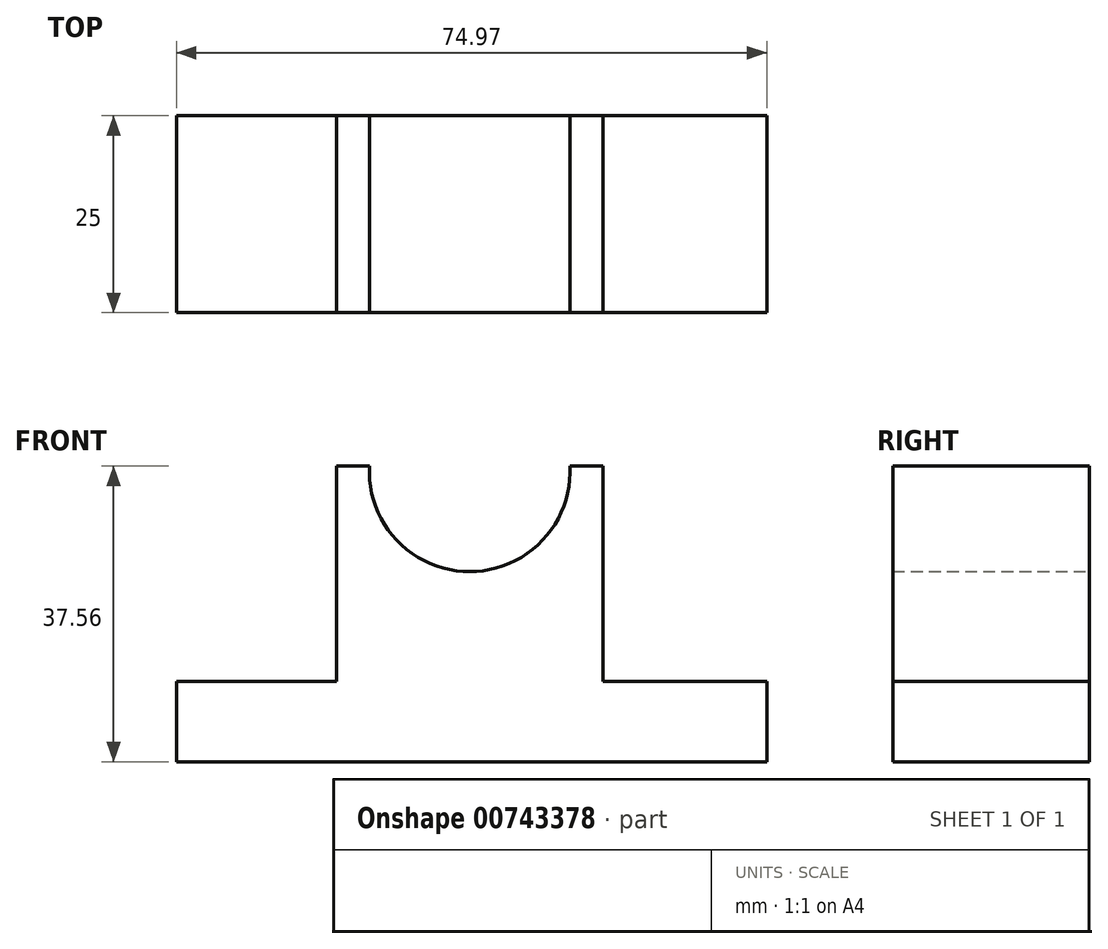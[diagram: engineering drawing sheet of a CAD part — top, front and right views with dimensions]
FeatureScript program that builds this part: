
annotation { "Feature Type Name" : "Feature", "Feature Type Description" : "" }
export const myFeature = defineFeature(function(context is Context, id is Id, definition is map)
    precondition{}
    {
        {
            var Q0;
            Q0=qCreatedBy(makeId("Front.planeOp"),FACE);
            var sketch = newSketch(context, id + "F0", { "sketchPlane" : qUnion([Q0])});
            skLineSegment(sketch, "E0", {"start": v(0, 0) * mm, "end": v(0, 10.22) * mm});
            skLineSegment(sketch, "E1", {"start": v(0, 0) * mm, "end": v(74.97, 0) * mm});
            skLineSegment(sketch, "E2", {"start": v(74.97, 0) * mm, "end": v(74.97, 10.22) * mm});
            skLineSegment(sketch, "E3", {"start": v(0, 10.22) * mm, "end": v(20.3, 10.22) * mm});
            skLineSegment(sketch, "E4", {"start": v(74.97, 10.22) * mm, "end": v(54.13, 10.22) * mm});
            skLineSegment(sketch, "E5", {"start": v(54.13, 10.22) * mm, "end": v(54.13, 37.56) * mm});
            skLineSegment(sketch, "E6", {"start": v(20.3, 10.22) * mm, "end": v(20.3, 37.56) * mm});
            skLineSegment(sketch, "E7", {"start": v(20.3, 37.56) * mm, "end": v(24.5, 37.56) * mm});
            skLineSegment(sketch, "E8", {"start": v(54.13, 37.56) * mm, "end": v(49.96, 37.56) * mm});
            skArc(sketch, "E9", {"start": v(24.5, 37.56) * mm, "mid": v(37.23, 24.15) * mm, "end": v(49.96, 37.56) * mm});
            skSolve(sketch);
        }
        {
            var Q0;
            Q0 = qSketchRegion(id + "F0", true);
            extrude(context, id + "F1", {"entities" : qUnion([Q0]), "depth" : 25 * mm, "offsetDistance" : 25 * mm});
        }
    });
